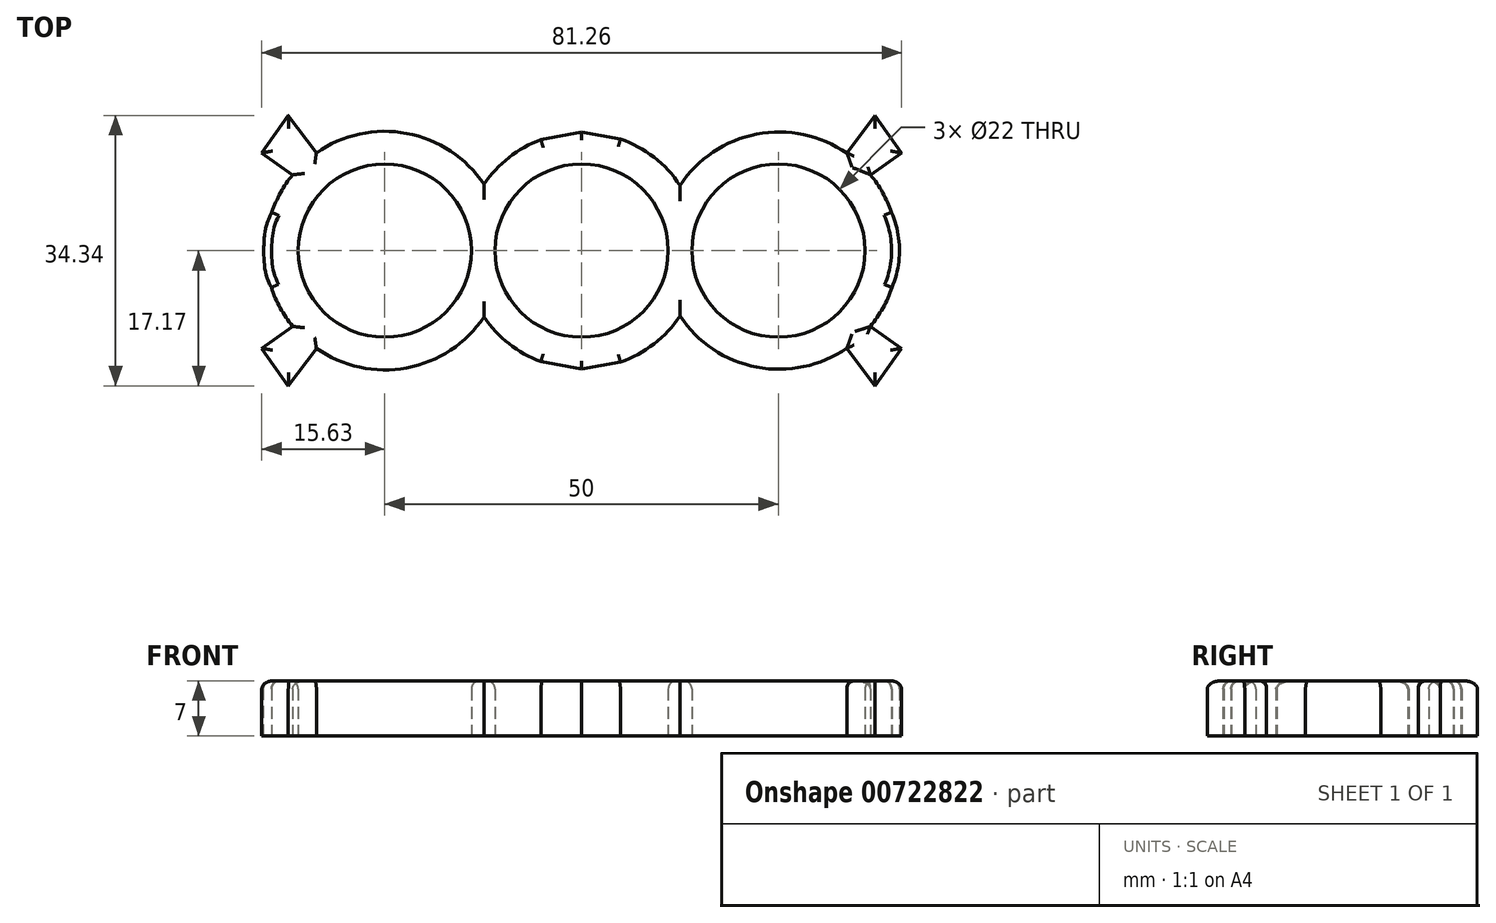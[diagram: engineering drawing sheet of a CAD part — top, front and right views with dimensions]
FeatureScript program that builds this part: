
annotation { "Feature Type Name" : "Feature", "Feature Type Description" : "" }
export const myFeature = defineFeature(function(context is Context, id is Id, definition is map)
    precondition{}
    {
        {
            var Q0;
            Q0=qCreatedBy(makeId("Top.planeOp"),FACE);
            var sketch = newSketch(context, id + "F0", { "sketchPlane" : qUnion([Q0])});
            skArc(sketch, "E0", {"start": v(0, 11) * mm, "mid": v(-11, 0) * mm, "end": v(0, -11) * mm});
            skArc(sketch, "E1", {"start": v(-12.4, -8.43) * mm, "mid": v(-9.23, -11.83) * mm, "end": v(-5.16, -14.08) * mm});
            skCircle(sketch, "E2", {"center": v(-25, 0) * mm, "radius": 11 * mm});
            skArc(sketch, "E3.trimOffspring", {"start": v(-12.4, 8.43) * mm, "mid": v(-22.21, 14.9) * mm, "end": v(-33.7, 12.41) * mm});
            skArc(sketch, "E4.trimOffspring", {"start": v(-5.16, 14.08) * mm, "mid": v(-9.23, 11.83) * mm, "end": v(-12.4, 8.43) * mm});
            skArc(sketch, "E5.MirrorCS", {"start": v(12.5, 8.3) * mm, "mid": v(22.34, 14.82) * mm, "end": v(33.87, 12.25) * mm});
            skCircle(sketch, "E6.MirrorC", {"center": v(25, 0) * mm, "radius": 11 * mm});
            skArc(sketch, "E7.MirrorCS", {"start": v(4.92, 14.17) * mm, "mid": v(9.2, 11.85) * mm, "end": v(12.5, 8.3) * mm});
            skArc(sketch, "E8.MirrorCS", {"start": v(12.5, -8.3) * mm, "mid": v(9.2, -11.85) * mm, "end": v(4.92, -14.17) * mm});
            skArc(sketch, "E9.MirrorCS", {"start": v(0, 11) * mm, "mid": v(11, 0) * mm, "end": v(0, -11) * mm});
            skLineSegment(sketch, "E10", {"start": v(0, 15.07) * mm, "end": v(-5.16, 14.08) * mm});
            skLineSegment(sketch, "E11", {"start": v(0, 15.07) * mm, "end": v(4.92, 14.17) * mm});
            skLineSegment(sketch, "E12.MirrorCS", {"start": v(0, -15.07) * mm, "end": v(-5.16, -14.08) * mm});
            skLineSegment(sketch, "E13.MirrorCS", {"start": v(0, -15.07) * mm, "end": v(4.92, -14.17) * mm});
            skPoint(sketch, "E14.orphan", {"position": v(0, 15) * mm});
            skArc(sketch, "E15.trimOffspring", {"start": v(39.41, -4.68) * mm, "mid": v(38.26, -7.33) * mm, "end": v(36.61, -9.7) * mm});
            skArc(sketch, "E16.trimOffspring", {"start": v(-39.41, -4.68) * mm, "mid": v(-38.3, -7.28) * mm, "end": v(-36.7, -9.63) * mm});
            skPoint(sketch, "E17.end.orphan", {"position": v(-40.38, 0) * mm});
            skPoint(sketch, "E18.MirrorCS.end.orphan", {"position": v(40.38, 0) * mm});
            skFitSpline(sketch, "E19", {"points": [v(-39.35, 4.86) * mm, v(-40.38, 0) * mm, v(-39.41, -4.68) * mm], "startDerivative": vector(-5.35, -9.58) * mm, "endDerivative": vector(5.26, -9.3) * mm});
            skFitSpline(sketch, "E20", {"points": [v(39.35, 4.86) * mm, v(40.38, 0) * mm, v(39.41, -4.68) * mm], "startDerivative": vector(4.22, -9.58) * mm, "endDerivative": vector(-4.13, -9.31) * mm});
            skLineSegment(sketch, "E21", {"start": v(-37.25, 17.17) * mm, "end": v(-33.7, 12.41) * mm});
            skLineSegment(sketch, "E22", {"start": v(-37.25, 17.17) * mm, "end": v(-40.63, 12.41) * mm});
            skLineSegment(sketch, "E23", {"start": v(-40.63, 12.41) * mm, "end": v(-36.7, 9.63) * mm});
            skLineSegment(sketch, "E24.MirrorCS", {"start": v(-40.63, -12.41) * mm, "end": v(-36.7, -9.63) * mm});
            skLineSegment(sketch, "E25.MirrorCS", {"start": v(-37.25, -17.17) * mm, "end": v(-40.63, -12.41) * mm});
            skLineSegment(sketch, "E26.MirrorCS", {"start": v(-37.25, -17.17) * mm, "end": v(-33.7, -12.41) * mm});
            skArc(sketch, "E27.trimOffspring", {"start": v(-36.7, 9.63) * mm, "mid": v(-38.24, 7.36) * mm, "end": v(-39.35, 4.86) * mm});
            skArc(sketch, "E28.trimOffspring", {"start": v(-33.7, -12.41) * mm, "mid": v(-22.21, -14.9) * mm, "end": v(-12.4, -8.43) * mm});
            skPoint(sketch, "E29.MirrorCS.end.orphan", {"position": v(33.7, 12.41) * mm});
            skPoint(sketch, "E29.MirrorCS.start.orphan", {"position": v(37.25, 17.17) * mm});
            skPoint(sketch, "E30.MirrorCS.end.orphan", {"position": v(40.63, 12.41) * mm});
            skPoint(sketch, "E31.MirrorCS.end.orphan", {"position": v(36.7, 9.63) * mm});
            skPoint(sketch, "E32.MirrorCS.end.orphan", {"position": v(36.7, -9.63) * mm});
            skPoint(sketch, "E32.MirrorCS.start.orphan", {"position": v(40.63, -12.41) * mm});
            skPoint(sketch, "E33.MirrorCS.start.orphan", {"position": v(37.25, -17.17) * mm});
            skPoint(sketch, "E34.MirrorCS.end.orphan", {"position": v(33.7, -12.41) * mm});
            skLineSegment(sketch, "E35.MirrorCS", {"start": v(37.25, 17.17) * mm, "end": v(33.7, 12.41) * mm});
            skLineSegment(sketch, "E36.MirrorCS", {"start": v(37.25, 17.17) * mm, "end": v(40.63, 12.41) * mm});
            skLineSegment(sketch, "E37.MirrorCS", {"start": v(40.63, 12.41) * mm, "end": v(36.7, 9.63) * mm});
            skLineSegment(sketch, "E38.MirrorCS", {"start": v(40.63, -12.41) * mm, "end": v(36.7, -9.63) * mm});
            skLineSegment(sketch, "E39.MirrorCS", {"start": v(37.25, -17.17) * mm, "end": v(40.63, -12.41) * mm});
            skLineSegment(sketch, "E40.MirrorCS", {"start": v(37.25, -17.17) * mm, "end": v(33.7, -12.41) * mm});
            skLineSegment(sketch, "E41", {"start": v(33.7, 12.41) * mm, "end": v(33.87, 12.25) * mm});
            skLineSegment(sketch, "E42", {"start": v(36.7, -9.63) * mm, "end": v(36.61, -9.7) * mm});
            skFitSpline(sketch, "E43", {"points": [v(33.7, 12.41) * mm, v(33.7, 10.04) * mm, v(36.7, 9.63) * mm], "startDerivative": vector(-1.33, -6.06) * mm, "endDerivative": vector(7.18, 0.35) * mm});
            skFitSpline(sketch, "E44", {"points": [v(36.7, -9.63) * mm, v(33.7, -9.63) * mm, v(33.7, -12.41) * mm], "startDerivative": vector(-7.41, 1.45) * mm, "endDerivative": vector(1.45, -7.08) * mm});
            skLineSegment(sketch, "E45.trimOffspring", {"start": v(36.62, 9.7) * mm, "end": v(36.7, 9.63) * mm});
            skArc(sketch, "E46.trimOffspring", {"start": v(36.62, 9.7) * mm, "mid": v(38.21, 7.41) * mm, "end": v(39.35, 4.86) * mm});
            skArc(sketch, "E47.trimOffspring", {"start": v(33.88, -12.24) * mm, "mid": v(22.35, -14.82) * mm, "end": v(12.5, -8.3) * mm});
            skLineSegment(sketch, "E48.trimOffspring", {"start": v(33.88, -12.24) * mm, "end": v(33.7, -12.41) * mm});
            skSolve(sketch);
        }
        {
            var Q0;
            Q0 = qSketchRegion(id + "F0", true);
            extrude(context, id + "F1", {"entities" : qUnion([Q0]), "depth" : 7 * mm, "offsetDistance" : 25 * mm});
        }
        {
            var Q0;
            Q0=makeQuery(id+"F1.opExtrude","CAP_EDGE",EDGE,{"disambiguationData":[OSD([sQuery(id+"F0.wireOp",EDGE,"E2")])],"isStart":false});
            var Q1;
            Q1=makeQuery(id+"F1.opExtrude","CAP_FACE",FACE,{"disambiguationData":[OSD([sQuery(id+"F0.wireOp",EDGE,"E0"),sQuery(id+"F0.wireOp",EDGE,"E1"),sQuery(id+"F0.wireOp",EDGE,"E2"),sQuery(id+"F0.wireOp",EDGE,"E3.trimOffspring"),sQuery(id+"F0.wireOp",EDGE,"E4.trimOffspring"),sQuery(id+"F0.wireOp",EDGE,"E5.MirrorCS"),sQuery(id+"F0.wireOp",EDGE,"E6.MirrorC"),sQuery(id+"F0.wireOp",EDGE,"2c85588b-1e82-4ad9-9dc9-baa7a524d6910.MirrorCS"),sQuery(id+"F0.wireOp",EDGE,"E9.MirrorCS"),sQuery(id+"F0.wireOp",EDGE,"E7.MirrorCS")])],"isStart":false});
            fillet(context, id + "F2", {"entities" : qUnion([Q0, Q1]), "radius" : 1 * mm, "tangentPropagation" : true, "allowEdgeOverflow" : false});
        }
    });
